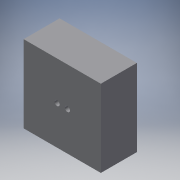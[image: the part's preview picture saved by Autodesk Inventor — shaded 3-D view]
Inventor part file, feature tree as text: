
AUTODESK INVENTOR PART (.ipt)
format: ipt  version: 2016 (Build 200138000, 138)  size: 2,065,920 bytes
history: native  units: mm
features: sketch x38, plane x28, fillet x17, extrude x13, chamfer x4, other x3, loft x1, mirror x1, move_body x1, boolean_combine x1, hole x1
ambient origin geometry x8: Origin, YZ Plane, XZ Plane, XY Plane, X Axis, Y Axis, Z Axis, Center Point
bodies: Solid1 (feature_tree), Solid2 (feature_tree)
feature tree (108):
  other  "Part5.ipt"
  sketch  "Sketch1"  dims[d1=8.0mm d2=7.0mm]
  plane  "Work Plane4"
  sketch  "Sketch2"  dims[d3=7.0mm d4=8.0mm d8=20.0mm d9=-3.490659mm d11=8.0mm d12=8.0mm d14=2.0mm d15=10.0mm d17=-1.745329mm d18=1.0mm d19=11.75mm]
  sketch  "Sketch3"  dims[d20=20.0mm d21=9.5mm]
  sketch  "Sketch4"  dims[d22=8.0mm d23=0.0mm d25=9.0mm]
  sketch  "Sketch5"  dims[d27=8.5mm d28=3.0mm]
  sketch  "Sketch6"  dims[d29=-1.745329mm d30=-3.490659mm d31=1.0mm d32=2.0mm d33=8.6mm]
  plane  "Work Plane5"
  sketch  "Sketch7"  dims[d34=8.5mm d35=7.0mm]
  plane  "Work Plane7"
  sketch  "Sketch8"  dims[d36=7.0mm d37=5.0mm d38=3.0mm]
  plane  "Work Plane8"
  sketch  "Sketch9"  dims[d39=17.0mm]
  plane  "Work Plane10"
  sketch  "Sketch10"  dims[d40=8.0mm]
  plane  "Work Plane11"
  plane  "Work Plane12"
  sketch  "Sketch11"  dims[d41=17.0mm]
  sketch  "Sketch12"  dims[d42=7.7mm]
  sketch  "Sketch13"  dims[d43=17.0mm]
  plane  "Work Plane13"
  plane  "Work Plane14"
  plane  "Work Plane15"
  plane  "Work Plane16"
  sketch  "Sketch14"  dims[d44=6.8mm]
  sketch  "Sketch15"  dims[d45=17.0mm]
  plane  "Work Plane20"
  sketch  "Sketch16"  dims[d46=5.0mm]
  sketch  "Sketch17"  dims[d47=2.0mm]
  sketch  "Sketch18"  dims[d48=17.0mm]
  sketch  "Sketch19"  dims[d49=2.0mm]
  plane  "Work Plane21"
  loft  "Loft1"
  extrude  "Extrusion1"  Depth=1.0mm
  fillet  "Fillet1"  [1 undecoded]
  fillet  "Fillet2"  Radius=8.0mm
  fillet  "Fillet3"  Radius=2.0mm
  fillet  "Fillet4"  Radius=10.0mm
  fillet  "Fillet5"  Radius=1.0mm
  fillet  "Fillet6"  Radius=11.75mm
  plane  "Work Plane23"
  plane  "Work Plane25"
  sketch  "Sketch22"  dims[d81=0.0mm d82=90.0deg d83=0.0mm d84=90.0deg]
  extrude  "Extrusion2"  Depth=9.5mm
  plane  "Work Plane26"
  sketch  "Sketch24"  dims[d86=6.0mm]
  sketch  "Sketch25"  dims[d87=6.0mm]
  extrude  "Extrusion3"  Depth=9.0mm
  extrude  "Extrusion4"  Depth=3.0mm
  sketch  "Sketch27"  dims[d89=135.0deg]
  extrude  "Extrusion5"  Depth=1.0mm
  sketch  "Sketch29"  dims[d91=45.0deg d92=15.0mm d93=0.0mm]
  extrude  "Extrusion6"  Depth=7.0mm
  extrude  "Extrusion7"  Depth=5.0mm
  mirror  "Mirror1"
  chamfer  "Chamfer1"  Angle=90.0deg  [1 undecoded]
  fillet  "Fillet7"  [1 undecoded]
  fillet  "Fillet8"  [1 undecoded]
  fillet  "Fillet9"  [1 undecoded]
  fillet  "Fillet10"  [1 undecoded]
  fillet  "Fillet11"  [1 undecoded]
  chamfer  "Chamfer2"  Angle=90.0deg  [1 undecoded]
  fillet  "Fillet12"  [1 undecoded]
  fillet  "Fillet13"  [1 undecoded]
  fillet  "Fillet14"  [1 undecoded]
  fillet  "Fillet15"  [1 undecoded]
  fillet  "Fillet16"  [1 undecoded]
  fillet  "Fillet17"  [1 undecoded]
  sketch  "Sketch31"  dims[d96=2.0mm d97=2.0mm]
  plane  "Work Plane27"
  extrude  "Extrusion9"  TaperAngle=0.0deg  [1 undecoded]
  extrude  "Extrusion10"  TaperAngle=0.0deg  [1 undecoded]
  chamfer  "Chamfer4"  Distance=15.0mm
  extrude  "Extrusion11"  Depth=2.0mm
  extrude  "Extrusion12"  Depth=2.0mm
  extrude  "Extrusion13"  Depth=2.0mm
  chamfer  "Chamfer5"  Distance=22.0mm Angle=90.0deg
  plane  "Work Plane28"
  move_body  "Move Body1"
  boolean_combine  "Combine1"
  extrude  "Extrusion15"  Depth=3.0mm
  hole  "Hole1"  [1 undecoded]
  plane  "Work Plane1"
  plane  "Work Plane2"
  plane  "Work Plane3"
  plane  "Work Plane6"
  plane  "Work Plane9"
  plane  "Work Plane17"
  plane  "Work Plane18"
  plane  "Work Plane19"
  sketch  "Sketch20"  dims[d50=2.0mm d51=0.0mm d52=90.0deg d53=0.0mm d54=90.0deg d55=0.0mm d56=90.0deg d57=0.0mm d58=90.0deg d59=0.0mm d60=90.0deg d61=0.0mm d62=90.0deg d63=0.0mm d64=90.0deg d65=0.0mm d66=90.0deg d67=0.0mm d68=90.0deg d69=0.0mm d70=90.0deg d71=0.0mm d72=90.0deg d73=0.0mm d74=90.0deg d75=0.0mm d76=90.0deg]
  sketch  "Sketch21"  dims[d77=0.0mm d78=90.0deg d79=0.0mm d80=90.0deg]
  plane  "Work Plane22"
  plane  "Work Plane24"
  sketch  "Sketch23"  dims[d85=0.3mm]
  sketch  "Sketch26"  dims[d88=2.0mm]
  sketch  "Sketch28"  dims[d90=2.0mm]
  sketch  "Sketch30"  dims[d94=2.0mm d95=2.0mm]
  sketch  "Sketch32"  dims[d98=2.0mm d99=2.0mm d100=90.0deg d101=22.0mm]
  sketch  "Sketch33"  dims[d102=12.217305mm d103=20.0mm d110=3.0mm]
  sketch  "Sketch34"  dims[d111=6.0mm d112=8.0mm]
  sketch  "Sketch35"  dims[d113=6.0mm]
  sketch  "Sketch36"  dims[d114=20.0mm d115=0.0mm]
  other  "Solid1::Part5.ipt"
  other  "TaggingFeature1"
  sketch  "Sketch38"  dims[d116=12.0mm]
  sketch  "Sketch39"  dims[d117=20.0mm d118=10.0mm d123=2.0mm d124=4.0mm d125=4.0mm d126=12.0mm d127=6.0mm d128=6.0mm d129=0.0mm d130=10.75mm d131=9.0mm d132=9.0mm d133=60.0mm d134=0.0mm d135=30.0mm d136=2.0mm d137=12.0mm d138=6.0mm d139=0.0mm d140=1.2mm d141=8.0mm d142=8.0mm d143=1.2mm d144=12.0mm d145=0.0mm d146=20.0mm d147=0.0mm d148=0.5mm d149=2.0mm d150=45.0deg d151=1.0mm d152=0.5mm d153=0.5mm d154=1.0mm d155=0.5mm d156=0.5mm d157=2.0mm d158=45.0deg d159=1.0mm d160=0.5mm d161=1.0mm d162=0.5mm d163=0.5mm d164=0.5mm d167=4.2mm d168=0.0mm d172=4.5mm d173=2.7mm d174=0.0mm d175=2.0mm d176=2.0mm d177=45.0deg d178=2.8mm d179=0.0mm d180=14.0mm d181=4.2mm d182=0.0mm d183=2.8mm d184=0.0mm d185=2.0mm d186=2.0mm d187=45.0deg d188=60.0deg d194=10.0mm d195=87.0mm d196=-61.0mm d197=-15.0mm d198=16.0mm d199=0.0mm d200=2.0mm d201=4.0mm d202=2.0mm d203=6.0mm d204=4.0mm d205=2.0mm d206=90.0deg d207=100.0mm d208=20.594885mm]
note: 17 required parameter values undecoded (feature->parameter linkage not recoverable at this tier; creation-order binding heuristic only, values carry confidence <= 0.55)
